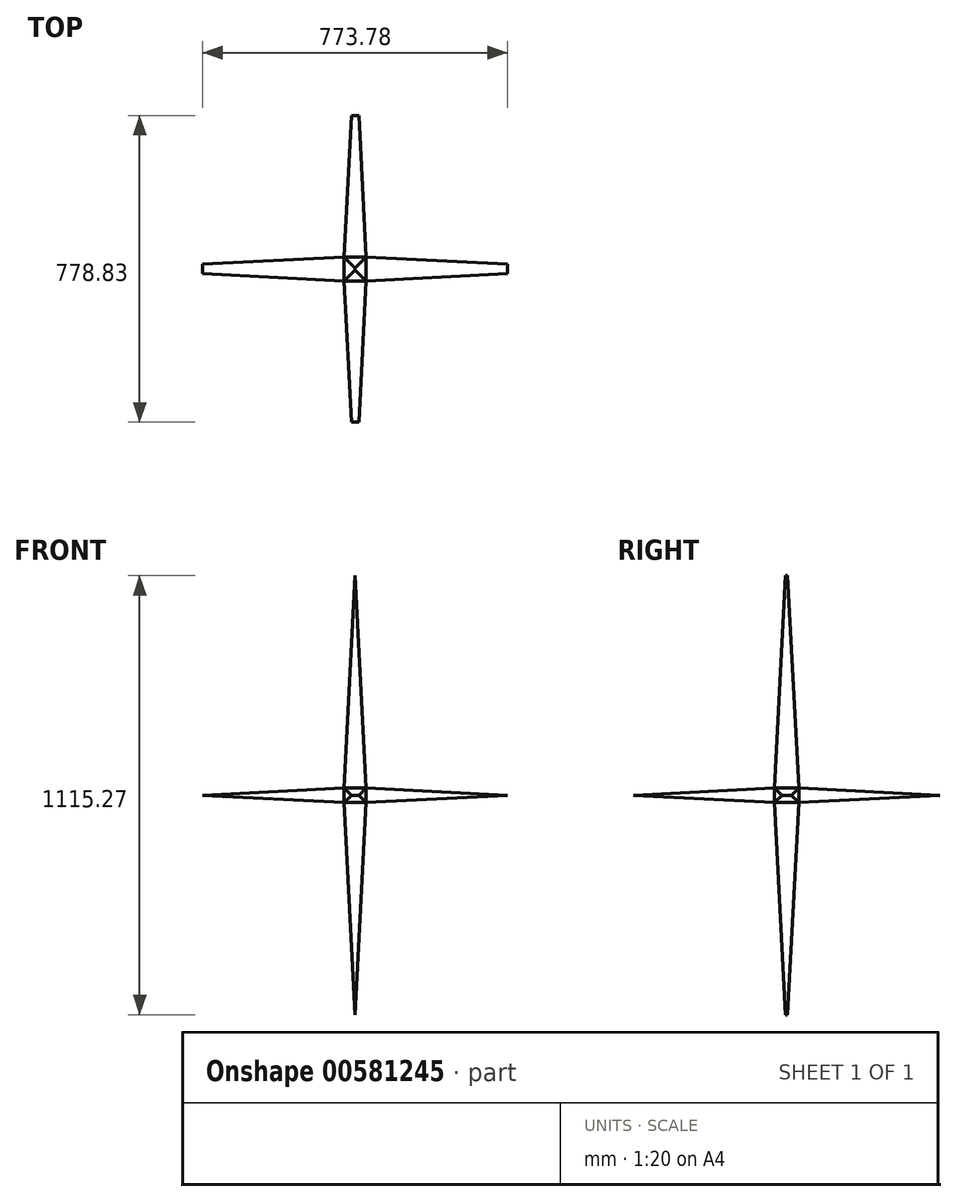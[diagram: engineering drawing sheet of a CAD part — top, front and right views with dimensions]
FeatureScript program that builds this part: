
annotation { "Feature Type Name" : "Feature", "Feature Type Description" : "" }
export const myFeature = defineFeature(function(context is Context, id is Id, definition is map)
    precondition{}
    {
        {
            var Q0;
            Q0=qCreatedBy(makeId("Top.planeOp"),FACE);
            var sketch = newSketch(context, id + "F0", { "sketchPlane" : qUnion([Q0])});
            skLineSegment(sketch, "E0.bottom", {"start": v(-26.12, 23.41) * mm, "end": v(30.36, 23.41) * mm});
            skLineSegment(sketch, "E0.top", {"start": v(-26.12, -38.12) * mm, "end": v(30.36, -38.12) * mm});
            skLineSegment(sketch, "E0.left", {"start": v(-26.12, 23.41) * mm, "end": v(-26.12, -38.12) * mm});
            skLineSegment(sketch, "E0.right", {"start": v(30.36, 23.41) * mm, "end": v(30.36, -38.12) * mm});
            skSolve(sketch);
        }
        {
            var Q0;
            Q0=makeQuery(id+"F0.imprint","IMPRINT",FACE,{"disambiguationData":[TD([[makeQuery(id+"F0.imprint","IMPRINT",EDGE,{"derivedFrom":sQuery(id+"F0.wireOp",EDGE,"E0.bottom")}),-1.0]])]});
            extrude(context, id + "F1", {"entities" : qUnion([Q0]), "depth" : 37.6 * mm, "offsetDistance" : 25.4 * mm});
        }
        {
            var Q0;
            Q0=makeQuery(id+"F1.opExtrude","CAP_FACE",FACE,{"disambiguationData":[OSD([sQuery(id+"F0.wireOp",EDGE,"E0.bottom"),sQuery(id+"F0.wireOp",EDGE,"E0.top"),sQuery(id+"F0.wireOp",EDGE,"E0.left"),sQuery(id+"F0.wireOp",EDGE,"E0.right")])],"isStart":false});
            var sketch = newSketch(context, id + "F2", { "sketchPlane" : qUnion([Q0])});
            skLineSegment(sketch, "E1.bottom", {"start": v(-26.12, -38.12) * mm, "end": v(30.36, -38.12) * mm});
            skLineSegment(sketch, "E1.top", {"start": v(-26.12, 23.41) * mm, "end": v(30.36, 23.41) * mm});
            skLineSegment(sketch, "E1.left", {"start": v(-26.12, -38.12) * mm, "end": v(-26.12, 23.41) * mm});
            skLineSegment(sketch, "E1.right", {"start": v(30.36, -38.12) * mm, "end": v(30.36, 23.41) * mm});
            skSolve(sketch);
        }
        {
            var Q0;
            Q0=makeQuery(id+"F2.imprint","IMPRINT",FACE,{"disambiguationData":[TD([[makeQuery(id+"F2.imprint","IMPRINT",EDGE,{"derivedFrom":sQuery(id+"F2.wireOp",EDGE,"E1.bottom")}),1.0]])]});
            extrude(context, id + "F3", {"entities" : qUnion([Q0]), "operationType" : NewBodyOperationType.ADD, "depth" : 1051.8 * mm, "offsetDistance" : 25.4 * mm, "hasDraft" : true, "draftAngle" : 3 * degree, "draftPullDirection" : true});
        }
        {
            var Q0;
            Q0=makeQuery(id+"F1.opExtrude","SWEPT_FACE",FACE,{"disambiguationData":[OSD([sQuery(id+"F0.wireOp",EDGE,"E0.right")])]});
            var sketch = newSketch(context, id + "F4", { "sketchPlane" : qUnion([Q0])});
            skLineSegment(sketch, "E2.bottom", {"start": v(-38.12, 37.6) * mm, "end": v(23.41, 37.6) * mm});
            skLineSegment(sketch, "E2.top", {"start": v(-38.12, 0) * mm, "end": v(23.41, 0) * mm});
            skLineSegment(sketch, "E2.left", {"start": v(-38.12, 37.6) * mm, "end": v(-38.12, 0) * mm});
            skLineSegment(sketch, "E2.right", {"start": v(23.41, 37.6) * mm, "end": v(23.41, 0) * mm});
            skSolve(sketch);
        }
        {
            var Q0;
            Q0=makeQuery(id+"F4.imprint","IMPRINT",FACE,{"disambiguationData":[TD([[makeQuery(id+"F4.imprint","IMPRINT",EDGE,{"derivedFrom":sQuery(id+"F4.wireOp",EDGE,"E2.bottom")}),1.0]])]});
            extrude(context, id + "F5", {"entities" : qUnion([Q0]), "operationType" : NewBodyOperationType.ADD, "depth" : 1120.14 * mm, "offsetDistance" : 25.4 * mm, "hasDraft" : true, "draftAngle" : 3 * degree, "draftPullDirection" : true});
        }
        {
            var Q0;
            Q0=makeQuery(id+"F1.opExtrude","SWEPT_FACE",FACE,{"disambiguationData":[OSD([sQuery(id+"F0.wireOp",EDGE,"E0.top")])]});
            var sketch = newSketch(context, id + "F6", { "sketchPlane" : qUnion([Q0])});
            skSolve(sketch);
        }
        {
            var Q0;
            {var subQ0=sQuery(id+"F0.wireOp",EDGE,"E0.top");Q0=makeQuery(id+"F6.imprint","IMPRINT",FACE,{"disambiguationData":[TD([[makeQuery(id+"F6.imprint","IMPRINT",EDGE,{"derivedFrom":makeQuery(id+"F1.opExtrude","CAP_EDGE",EDGE,{"disambiguationData":[OSD([subQ0])],"isStart":true})}),1.0]])]});}
            extrude(context, id + "F7", {"entities" : qUnion([Q0]), "operationType" : NewBodyOperationType.ADD, "depth" : 563.88 * mm, "offsetDistance" : 25.4 * mm, "hasDraft" : true, "draftAngle" : 3 * degree, "draftPullDirection" : true});
        }
        {
            var Q0;
            Q0=makeQuery(id+"F1.opExtrude","SWEPT_FACE",FACE,{"disambiguationData":[OSD([sQuery(id+"F0.wireOp",EDGE,"E0.left")])]});
            var sketch = newSketch(context, id + "F8", { "sketchPlane" : qUnion([Q0])});
            skSolve(sketch);
        }
        {
            var Q0;
            Q0=makeQuery(id+"F1.opExtrude","SWEPT_FACE",FACE,{"disambiguationData":[OSD([sQuery(id+"F0.wireOp",EDGE,"E0.bottom")])]});
            extrude(context, id + "F9", {"entities" : qUnion([Q0]), "operationType" : NewBodyOperationType.ADD, "depth" : 660.4 * mm, "offsetDistance" : 25.4 * mm, "hasDraft" : true, "draftAngle" : 3 * degree, "draftPullDirection" : true});
        }
        {
            var Q0;
            {var subQ0=sQuery(id+"F0.wireOp",EDGE,"E0.left");Q0=makeQuery(id+"F8.imprint","IMPRINT",FACE,{"disambiguationData":[TD([[makeQuery(id+"F8.imprint","IMPRINT",EDGE,{"derivedFrom":makeQuery(id+"F1.opExtrude","CAP_EDGE",EDGE,{"disambiguationData":[OSD([subQ0])],"isStart":true})}),1.0]])]});}
            var sketch = newSketch(context, id + "F10", { "sketchPlane" : qUnion([Q0])});
            skSolve(sketch);
        }
        {
            var Q0;
            {var subQ0=sQuery(id+"F0.wireOp",EDGE,"E0.left");Q0=makeQuery(id+"F10.imprint","IMPRINT",FACE,{"disambiguationData":[TD([[makeQuery(id+"F10.imprint","IMPRINT",EDGE,{"derivedFrom":makeQuery(id+"F8.imprint","IMPRINT",EDGE,{"derivedFrom":makeQuery(id+"F1.opExtrude","CAP_EDGE",EDGE,{"disambiguationData":[OSD([subQ0])],"isStart":true})})}),1.0]])]});}
            extrude(context, id + "F11", {"entities" : qUnion([Q0]), "operationType" : NewBodyOperationType.ADD, "depth" : 642.62 * mm, "offsetDistance" : 25.4 * mm, "hasDraft" : true, "draftAngle" : 3 * degree, "draftPullDirection" : true});
        }
        {
            var Q0;
            Q0=makeQuery(id+"F1.opExtrude","CAP_FACE",FACE,{"disambiguationData":[OSD([sQuery(id+"F0.wireOp",EDGE,"E0.bottom"),sQuery(id+"F0.wireOp",EDGE,"E0.top"),sQuery(id+"F0.wireOp",EDGE,"E0.left"),sQuery(id+"F0.wireOp",EDGE,"E0.right")])],"isStart":true});
            var sketch = newSketch(context, id + "F12", { "sketchPlane" : qUnion([Q0])});
            skSolve(sketch);
        }
        {
            var Q0;
            Q0=makeQuery(id+"F12.imprint","IMPRINT",FACE,{"disambiguationData":[TD([[makeQuery(id+"F12.imprint","IMPRINT",EDGE,{"derivedFrom":makeQuery(id+"F5.boolean.opBoolean","MERGE",EDGE,{"derivedFrom":[makeQuery(id+"F1.opExtrude","CAP_EDGE",EDGE,{"disambiguationData":[OSD([sQuery(id+"F0.wireOp",EDGE,"E0.right")])],"isStart":true}),makeQuery(id+"F5.opExtrude","CAP_EDGE",EDGE,{"disambiguationData":[OSD([sQuery(id+"F4.wireOp",EDGE,"E2.top")])],"isStart":true})]})}),1.0]])]});
            extrude(context, id + "F13", {"entities" : qUnion([Q0]), "operationType" : NewBodyOperationType.ADD, "depth" : 2240.28 * mm, "offsetDistance" : 25.4 * mm, "hasDraft" : true, "draftAngle" : 3 * degree, "draftPullDirection" : true});
        }
    });
